# Revit family: Shower_Arm-GROHE-Relexa-27412_Series
name_source: partatom
category: Plumbing Fixtures
units: mm (PartAtom-declared; Revit-internal decimal feet)

## family parameters
Cut with Voids When Loaded = No
Host = Face
OmniClass Number = 23.45.05.14.17
OmniClass Title = Showers
Part Type = Normal
Room Calculation Point = No
Round Connector Dimension = Use Diameter
Shared = Yes

## types (5) — shared parameters
Assembly Code = D2090800
CWFU = 3
Default Elevation = 0"
Description = Relexa
Diameter = 2 9/16"
HWFU = 3
IAPMO Compliance = ASME A112.18.1/CSA B125.1
Installation Type = Wall Mounted
Length = 6 1/4"
Manufacturer = Grohe
Price = Prices may vary. Please consult Manufacturer Representative for most up-to-date price list.
Product Documentation Link = https://lixil.cdn.celum.cloud
Product Page URL = https://www.grohe.us
Revised Date = 06/22/2023
Tempered Connection Diameter = 1/2"
Tempered Connection Radius = 1/4"
Tempered Water Connection = Yes
URL = https://www.grohe.us
Vent Connection = No
WFU = 4
Waste Connection = No
Width = 1 5/8"

## per-type parameters (varying)
| type | CW Connection | Finish | HW Connection | Material |
| 27412000 | No | Brass-Grohe-000-StarLight Chrome | No | Brass-Grohe-000-StarLight Chrome |
| 27412EN0 | Yes | Brass-Grohe-EN0-Brushed Nickel Infinity Finish | Yes | Brass-Grohe-EN0-Brushed Nickel Infinity Finish |
| 27412GN0 | Yes | Brass-Grohe-GN0-Brushed Cool Sunrise | Yes | Brass-Grohe-GN0-Brushed Cool Sunrise |
| 27412A00 | Yes | Brass-Grohe-A00-Hard Graphite | Yes | Brass-Grohe-A00-Hard Graphite |
| 27412BE0 | Yes | Brass-Grohe-BE0-Polished Nickel Infinity Finish | Yes | Brass-Grohe-BE0-Polished Nickel Infinity Finish |

note: column(s) folded — value = type name in every type: Model

## geometry (parser evidence)
native form markers: Sweep x3
no freeform markers — native parametric forms only
